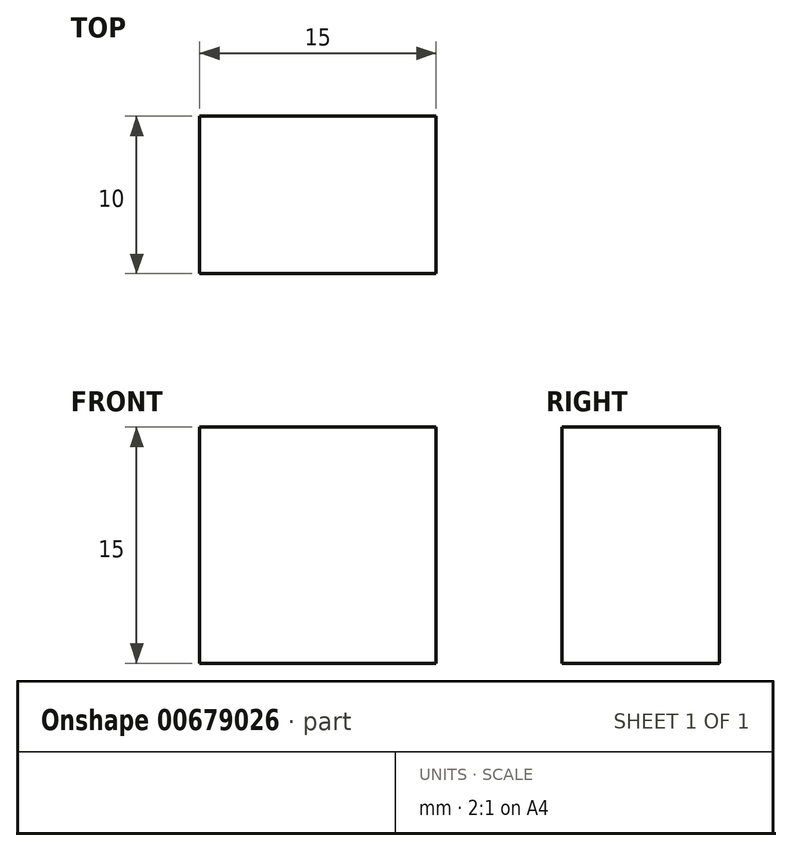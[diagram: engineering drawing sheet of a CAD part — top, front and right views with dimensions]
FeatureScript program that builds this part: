
annotation { "Feature Type Name" : "Feature", "Feature Type Description" : "" }
export const myFeature = defineFeature(function(context is Context, id is Id, definition is map)
    precondition{}
    {
        {
            var Q0;
            Q0=qCreatedBy(makeId("Front.planeOp"),FACE);
            var sketch = newSketch(context, id + "F0", { "sketchPlane" : qUnion([Q0])});
            skLineSegment(sketch, "E0.bottom", {"start": v(0, 0) * mm, "end": v(-15, 0) * mm});
            skLineSegment(sketch, "E0.top", {"start": v(0, 15) * mm, "end": v(-15, 15) * mm});
            skLineSegment(sketch, "E0.left", {"start": v(0, 0) * mm, "end": v(0, 15) * mm});
            skLineSegment(sketch, "E0.right", {"start": v(-15, 0) * mm, "end": v(-15, 15) * mm});
            skSolve(sketch);
        }
        {
            var Q0;
            Q0=makeQuery(id+"F0.imprint","IMPRINT",FACE,{"disambiguationData":[TD([[makeQuery(id+"F0.imprint","IMPRINT",EDGE,{"derivedFrom":sQuery(id+"F0.wireOp",EDGE,"E0.bottom")}),-1.0]])]});
            extrude(context, id + "F1", {"entities" : qUnion([Q0]), "depth" : 10 * mm, "offsetDistance" : 25 * mm});
        }
    });
